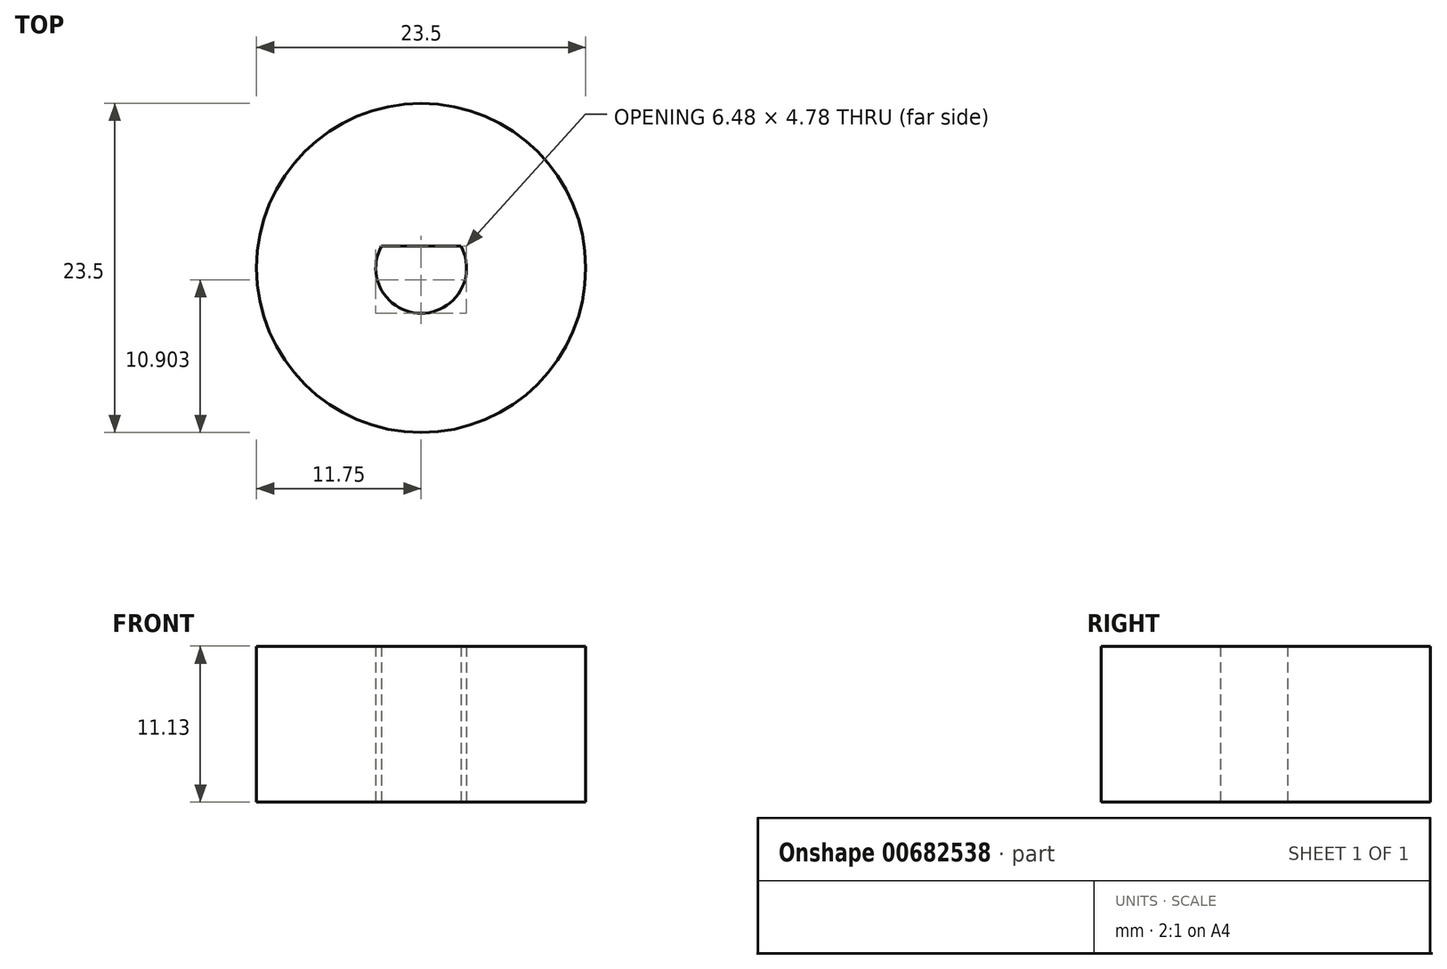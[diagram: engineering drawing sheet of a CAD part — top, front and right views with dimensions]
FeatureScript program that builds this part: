
annotation { "Feature Type Name" : "Feature", "Feature Type Description" : "" }
export const myFeature = defineFeature(function(context is Context, id is Id, definition is map)
    precondition{}
    {
        {
            var Q0;
            Q0=qCreatedBy(makeId("Top.planeOp"),FACE);
            var sketch = newSketch(context, id + "F0", { "sketchPlane" : qUnion([Q0])});
            skCircle(sketch, "E0", {"center": v(0, 0) * mm, "radius": 11.75 * mm});
            skCircle(sketch, "E1", {"center": v(0, 0) * mm, "radius": 3.24 * mm});
            skLineSegment(sketch, "E2.0", {"start": v(2.85, 1.54) * mm, "end": v(-2.85, 1.54) * mm});
            skSolve(sketch);
        }
        {
            var Q0;
            Q0=makeQuery(id+"F0.imprint","IMPRINT",FACE,{"disambiguationData":[TD([[makeQuery(id+"F0.imprint","IMPRINT",EDGE,{"derivedFrom":sQuery(id+"F0.wireOp",EDGE,"E0")}),1.0]])]});
            var Q1;
            {var subQ0=sQuery(id+"F0.wireOp",EDGE,"E2.0");Q1=makeQuery(id+"F0.imprint","IMPRINT",FACE,{"disambiguationData":[TD([[makeQuery(id+"F0.imprint","IMPRINT",EDGE,{"derivedFrom":subQ0}),-1.0]])]});}
            extrude(context, id + "F1", {"entities" : qUnion([Q0, Q1]), "depth" : 11.13 * mm, "offsetDistance" : 25.4 * mm});
        }
    });
